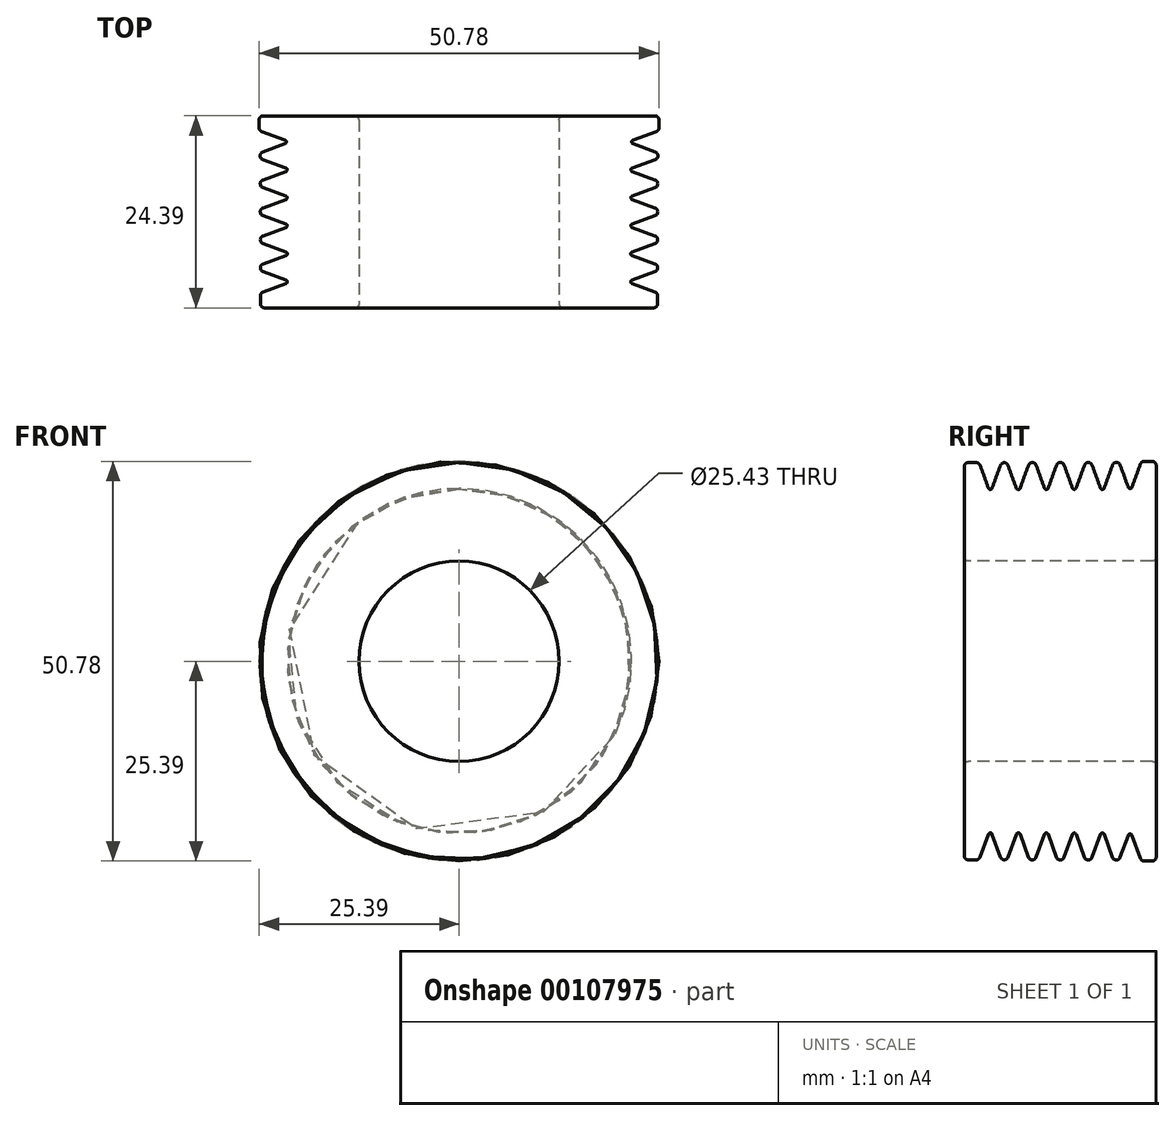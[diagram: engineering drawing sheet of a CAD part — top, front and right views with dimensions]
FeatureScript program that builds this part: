
annotation { "Feature Type Name" : "Feature", "Feature Type Description" : "" }
export const myFeature = defineFeature(function(context is Context, id is Id, definition is map)
    precondition{}
    {
        {
            var Q0;
            Q0=qCreatedBy(makeId("Front.planeOp"),FACE);
            var sketch = newSketch(context, id + "F0", { "sketchPlane" : qUnion([Q0])});
            skCircle(sketch, "E0", {"center": v(0, 0) * mm, "radius": 25.4 * mm});
            skCircle(sketch, "E1", {"center": v(0, 0) * mm, "radius": 12.7 * mm});
            skSolve(sketch);
        }
        {
            var Q0;
            Q0=qCreatedBy(makeId("Right.planeOp"),FACE);
            var sketch = newSketch(context, id + "F1", { "sketchPlane" : qUnion([Q0])});
            skLineSegment(sketch, "E2.bottom", {"start": v(0.03, 12.72) * mm, "end": v(-24.36, 12.72) * mm});
            skLineSegment(sketch, "E2.right", {"start": v(-24.36, 12.72) * mm, "end": v(-24.36, 25.23) * mm});
            skArc(sketch, "E3", {"start": v(-3.52, 22.1) * mm, "mid": v(-3.51, 22.08) * mm, "end": v(-3.5, 22.07) * mm});
            skLineSegment(sketch, "E4", {"start": v(-3.52, 22.1) * mm, "end": v(-4.55, 24.93) * mm});
            skLineSegment(sketch, "E5", {"start": v(-5.5, 24.93) * mm, "end": v(-6.58, 22) * mm});
            skArc(sketch, "E6", {"start": v(-4.55, 24.93) * mm, "mid": v(-5.03, 25.27) * mm, "end": v(-5.5, 24.93) * mm});
            skLineSegment(sketch, "E7", {"start": v(-7.05, 22) * mm, "end": v(-8.12, 24.91) * mm});
            skLineSegment(sketch, "E8", {"start": v(-9.07, 24.91) * mm, "end": v(-10.13, 22) * mm});
            skArc(sketch, "E9", {"start": v(-7.05, 22) * mm, "mid": v(-6.81, 21.83) * mm, "end": v(-6.58, 22) * mm});
            skArc(sketch, "E10", {"start": v(-10.61, 22) * mm, "mid": v(-10.37, 21.83) * mm, "end": v(-10.13, 22) * mm});
            skArc(sketch, "E11", {"start": v(-8.12, 24.91) * mm, "mid": v(-8.6, 25.25) * mm, "end": v(-9.07, 24.91) * mm});
            skLineSegment(sketch, "E12", {"start": v(-10.61, 22) * mm, "end": v(-11.67, 24.91) * mm});
            skLineSegment(sketch, "E13", {"start": v(-12.63, 24.91) * mm, "end": v(-13.69, 22) * mm});
            skArc(sketch, "E14", {"start": v(-11.67, 24.91) * mm, "mid": v(-12.15, 25.25) * mm, "end": v(-12.63, 24.91) * mm});
            skLineSegment(sketch, "E15", {"start": v(-10.6, 22) * mm, "end": v(-11.67, 24.91) * mm});
            skArc(sketch, "E16", {"start": v(-10.6, 22) * mm, "mid": v(-10.52, 21.87) * mm, "end": v(-10.37, 21.83) * mm});
            skArc(sketch, "E17", {"start": v(-14.17, 22) * mm, "mid": v(-13.93, 21.83) * mm, "end": v(-13.69, 22) * mm});
            skLineSegment(sketch, "E18", {"start": v(-14.17, 22) * mm, "end": v(-15.23, 24.9) * mm});
            skLineSegment(sketch, "E19", {"start": v(-16.18, 24.9) * mm, "end": v(-17.25, 21.97) * mm});
            skArc(sketch, "E20", {"start": v(-15.23, 24.9) * mm, "mid": v(-15.7, 25.24) * mm, "end": v(-16.18, 24.9) * mm});
            skLineSegment(sketch, "E21", {"start": v(-17.73, 21.97) * mm, "end": v(-18.8, 24.9) * mm});
            skLineSegment(sketch, "E22", {"start": v(-19.75, 24.9) * mm, "end": v(-20.8, 21.98) * mm});
            skArc(sketch, "E23", {"start": v(-17.73, 21.97) * mm, "mid": v(-17.49, 21.8) * mm, "end": v(-17.25, 21.97) * mm});
            skArc(sketch, "E24", {"start": v(-21.29, 21.98) * mm, "mid": v(-21.05, 21.81) * mm, "end": v(-20.8, 21.98) * mm});
            skArc(sketch, "E25", {"start": v(-18.8, 24.9) * mm, "mid": v(-19.27, 25.23) * mm, "end": v(-19.75, 24.9) * mm});
            skLineSegment(sketch, "E26", {"start": v(-21.29, 21.98) * mm, "end": v(-22.35, 24.9) * mm});
            skLineSegment(sketch, "E27", {"start": v(-24.36, 21.98) * mm, "end": v(-24.37, 21.97) * mm});
            skArc(sketch, "E28", {"start": v(-22.35, 24.9) * mm, "mid": v(-22.53, 25.14) * mm, "end": v(-22.82, 25.23) * mm});
            skLineSegment(sketch, "E29", {"start": v(-21.28, 21.97) * mm, "end": v(-22.35, 24.9) * mm});
            skArc(sketch, "E30", {"start": v(-21.28, 21.97) * mm, "mid": v(-21.2, 21.85) * mm, "end": v(-21.05, 21.8) * mm});
            skPoint(sketch, "E31.orphan", {"position": v(-3.5, 23) * mm});
            skPoint(sketch, "E32.orphan", {"position": v(-24.36, 23) * mm});
            skArc(sketch, "E33", {"start": v(-3.5, 22.07) * mm, "mid": v(-3.26, 21.94) * mm, "end": v(-3.04, 22.1) * mm});
            skLineSegment(sketch, "E34", {"start": v(-1.97, 25.06) * mm, "end": v(-3.04, 22.1) * mm});
            skLineSegment(sketch, "E35", {"start": v(-22.82, 25.23) * mm, "end": v(-24.36, 25.23) * mm});
            skArc(sketch, "E36", {"start": v(-1.49, 25.4) * mm, "mid": v(-1.78, 25.3) * mm, "end": v(-1.97, 25.06) * mm});
            skLineSegment(sketch, "E37", {"start": v(-1.49, 25.4) * mm, "end": v(0.03, 25.4) * mm});
            skLineSegment(sketch, "E38", {"start": v(0.03, 25.4) * mm, "end": v(0.03, 12.72) * mm});
            skPoint(sketch, "E39.orphan", {"position": v(-3.5, 12.72) * mm});
            skSolve(sketch);
        }
        {
            var Q0;
            Q0=makeQuery(id+"F1.imprint","IMPRINT",FACE,{"disambiguationData":[TD([[makeQuery(id+"F1.imprint","IMPRINT",EDGE,{"derivedFrom":sQuery(id+"F1.wireOp",EDGE,"E2.bottom")}),-1.0]])]});
            var Q1;
            Q1=sQuery(id+"F0.wireOp",EDGE,"E0");
            sweep(context, id + "F2", {"profiles" : qUnion([Q0]), "path" : qUnion([Q1])});
        }
        {
            var Q0;
            Q0=makeQuery(id+"F2.opSweep","SWEPT_FACE",FACE,{"disambiguationData":[OSD([sQuery(id+"F0.wireOp",EDGE,"E0"),sQuery(id+"F1.wireOp",EDGE,"E37")])]});
            var Q1;
            Q1=makeQuery(id+"F2.opSweep","SWEPT_EDGE",EDGE,{"disambiguationData":[OSD([sQuery(id+"F0.wireOp",EDGE,"E0"),sQuery(id+"F1.wireOp",EDGE,"E37"),sQuery(id+"F1.wireOp",EDGE,"E38")])]});
            var Q2;
            Q2=makeQuery(id+"F2.opSweep","SWEPT_FACE",FACE,{"disambiguationData":[OSD([sQuery(id+"F0.wireOp",EDGE,"E0"),sQuery(id+"F1.wireOp",EDGE,"E35")])]});
            var Q3;
            Q3=makeQuery(id+"F2.opSweep","SWEPT_EDGE",EDGE,{"disambiguationData":[OSD([sQuery(id+"F0.wireOp",EDGE,"E0"),sQuery(id+"F1.wireOp",EDGE,"E2.right"),sQuery(id+"F1.wireOp",EDGE,"E35")])]});
            var Q4;
            Q4=makeQuery(id+"FlnjXRKS8wczgzD_1.opExtrude","CAP_EDGE",EDGE,{"disambiguationData":[OSD([sQuery(id+"F0.wireOp",EDGE,"E0")])],"isStart":true});
            var Q5;
            Q5=makeQuery(id+"F2.opSweep","SWEPT_EDGE",EDGE,{"disambiguationData":[OSD([sQuery(id+"F0.wireOp",EDGE,"E0"),sQuery(id+"F1.wireOp",EDGE,"E2.bottom"),sQuery(id+"F1.wireOp",EDGE,"E38")])]});
            var Q6;
            Q6=makeQuery(id+"F2.opSweep","SWEPT_EDGE",EDGE,{"disambiguationData":[OSD([sQuery(id+"F0.wireOp",EDGE,"E0"),sQuery(id+"F1.wireOp",EDGE,"E2.bottom"),sQuery(id+"F1.wireOp",EDGE,"E2.right")])]});
            fillet(context, id + "F3", {"entities" : qUnion([Q0, Q1, Q2, Q3, Q4, Q5, Q6]), "radius" : 0.5 * mm, "tangentPropagation" : true, "allowEdgeOverflow" : false});
        }
    });
